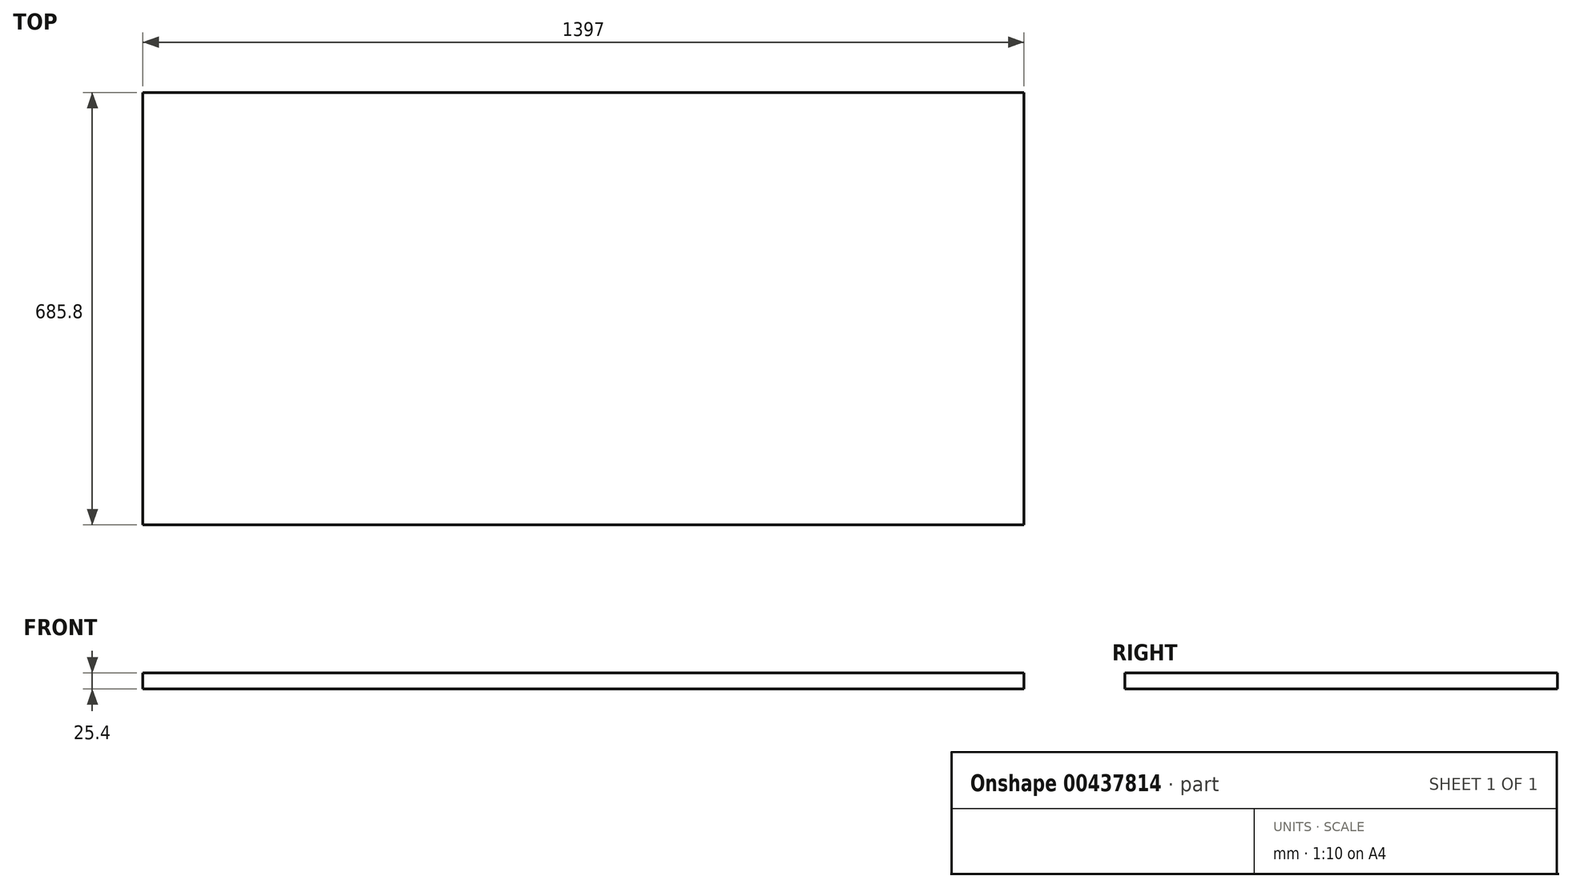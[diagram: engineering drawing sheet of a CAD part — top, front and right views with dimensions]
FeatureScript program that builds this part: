
annotation { "Feature Type Name" : "Feature", "Feature Type Description" : "" }
export const myFeature = defineFeature(function(context is Context, id is Id, definition is map)
    precondition{}
    {
        {
            var Q0;
            Q0=qCreatedBy(makeId("Top.planeOp"),FACE);
            var sketch = newSketch(context, id + "F0", { "sketchPlane" : qUnion([Q0])});
            skLineSegment(sketch, "E0.bottom", {"start": v(-685.4, -292.04) * mm, "end": v(711.6, -292.04) * mm});
            skLineSegment(sketch, "E0.top", {"start": v(-685.4, 393.76) * mm, "end": v(711.6, 393.76) * mm});
            skLineSegment(sketch, "E0.left", {"start": v(-685.4, -292.04) * mm, "end": v(-685.4, 393.76) * mm});
            skLineSegment(sketch, "E0.right", {"start": v(711.6, -292.04) * mm, "end": v(711.6, 393.76) * mm});
            skSolve(sketch);
        }
        {
            var Q0;
            Q0=makeQuery(id+"F0.imprint","IMPRINT",FACE,{"disambiguationData":[TD([[makeQuery(id+"F0.imprint","IMPRINT",EDGE,{"derivedFrom":sQuery(id+"F0.wireOp",EDGE,"E0.bottom")}),1.0]])]});
            extrude(context, id + "F1", {"entities" : qUnion([Q0]), "depth" : 25.4 * mm});
        }
    });
